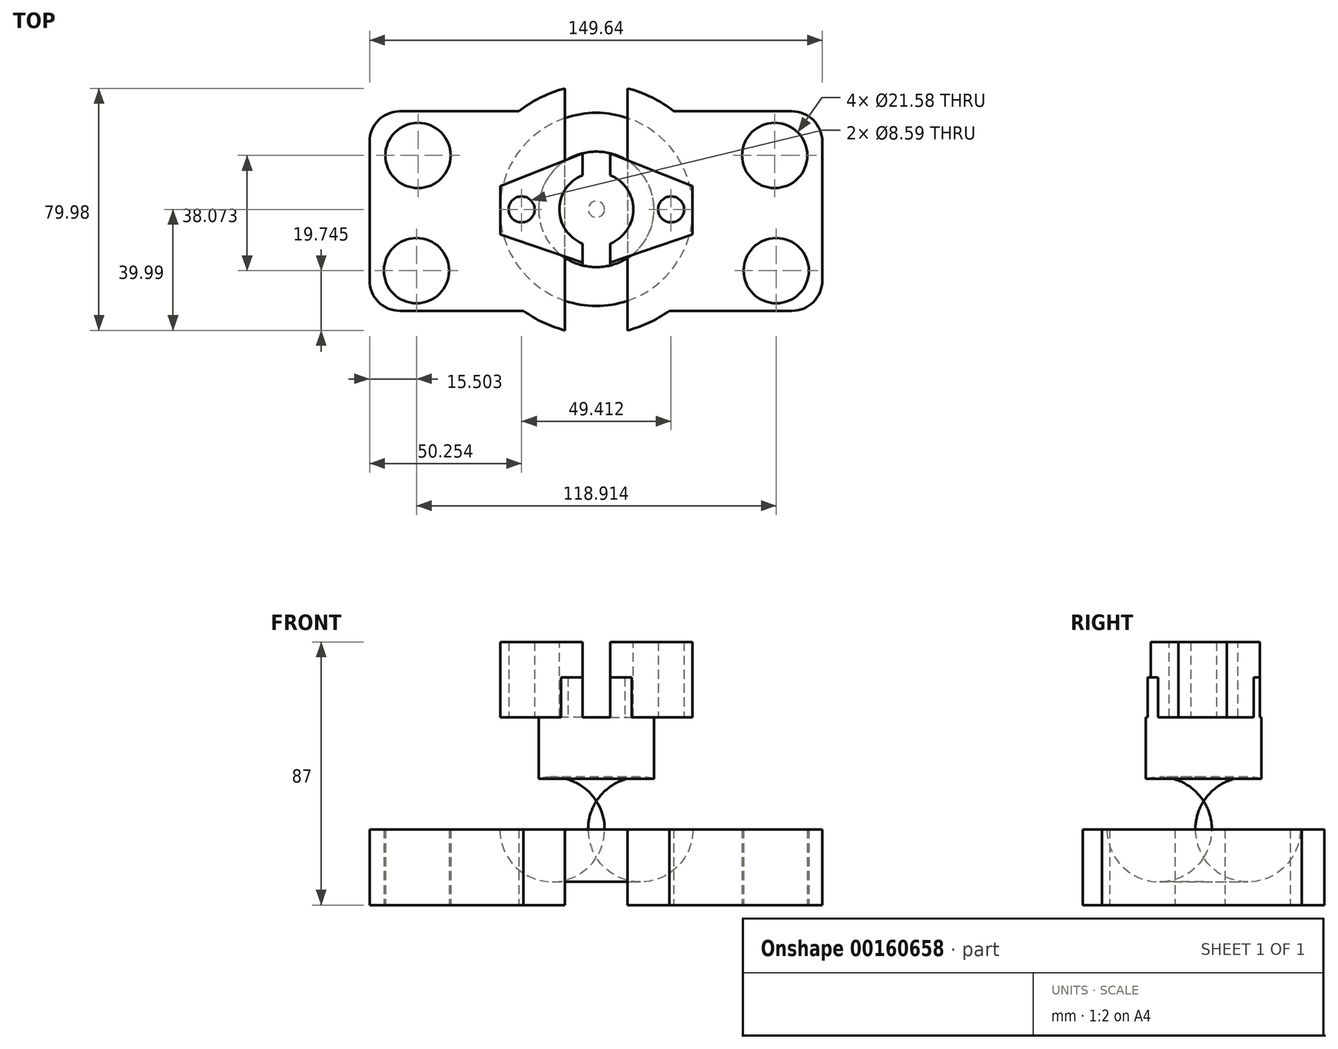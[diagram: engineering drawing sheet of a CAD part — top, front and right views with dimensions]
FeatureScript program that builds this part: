
annotation { "Feature Type Name" : "Feature", "Feature Type Description" : "" }
export const myFeature = defineFeature(function(context is Context, id is Id, definition is map)
    precondition{}
    {
        {
            var Q0;
            Q0=qCreatedBy(makeId("Top.planeOp"),FACE);
            var sketch = newSketch(context, id + "F0", { "sketchPlane" : qUnion([Q0])});
            skCircle(sketch, "E0", {"center": v(0, 0) * mm, "radius": 41.3 * mm});
            skLineSegment(sketch, "E1.bottom", {"start": v(-74.96, 32.43) * mm, "end": v(74.68, 32.43) * mm});
            skLineSegment(sketch, "E1.top", {"start": v(-74.96, -33.55) * mm, "end": v(74.68, -33.55) * mm});
            skLineSegment(sketch, "E1.left", {"start": v(-74.96, 32.43) * mm, "end": v(-74.96, -33.55) * mm});
            skLineSegment(sketch, "E1.right", {"start": v(74.68, 32.43) * mm, "end": v(74.68, -33.55) * mm});
            skCircle(sketch, "E2", {"center": v(-58.96, 17.83) * mm, "radius": 10.79 * mm});
            skCircle(sketch, "E3", {"center": v(-59.46, -20.25) * mm, "radius": 10.79 * mm});
            skCircle(sketch, "E4.MirrorC", {"center": v(59.46, -20.25) * mm, "radius": 10.79 * mm});
            skCircle(sketch, "E5.MirrorC", {"center": v(58.96, 17.83) * mm, "radius": 10.79 * mm});
            skLineSegment(sketch, "E6", {"start": v(-10.36, 40) * mm, "end": v(-10.36, 0) * mm});
            skLineSegment(sketch, "E7.MirrorCS", {"start": v(10.36, 40) * mm, "end": v(10.36, 0) * mm});
            skLineSegment(sketch, "E8", {"start": v(-10.36, 0) * mm, "end": v(10.36, 0) * mm});
            skLineSegment(sketch, "E9.MirrorCS", {"start": v(-10.36, -40) * mm, "end": v(-10.36, 0) * mm});
            skLineSegment(sketch, "E10.MirrorCS", {"start": v(10.36, -40) * mm, "end": v(10.36, 0) * mm});
            skSolve(sketch);
        }
        {
            var Q0;
            {var subQ0=sQuery(id+"F0.wireOp",EDGE,"E1.left");Q0=makeQuery(id+"F0.imprint","IMPRINT",FACE,{"disambiguationData":[TD([[makeQuery(id+"F0.imprint","IMPRINT",EDGE,{"derivedFrom":subQ0}),1.0]])]});}
            var Q1;
            {var subQ1=sQuery(id+"F0.wireOp",EDGE,"E0");var subQ7=sQuery(id+"F0.wireOp",EDGE,"E1.bottom");var subQ9=makeQuery(id+"F0.imprint","INTERSECT",VERTEX,{"disambiguationData":[OD(1.0)],"derivedFrom":[subQ1,subQ7]});Q1=makeQuery(id+"F0.imprint","IMPRINT",FACE,{"disambiguationData":[TD([[makeQuery(id+"F0.imprint","IMPRINT",EDGE,{"disambiguationData":[TD([[subQ9,-1.0]])],"derivedFrom":subQ1}),1.0]])]});}
            var Q2;
            {var subQ3=sQuery(id+"F0.wireOp",EDGE,"E1.bottom");var subQ6=sQuery(id+"F0.wireOp",EDGE,"E0");var subQ9=makeQuery(id+"F0.imprint","INTERSECT",VERTEX,{"disambiguationData":[OD(0.0)],"derivedFrom":[subQ6,subQ3]});Q2=makeQuery(id+"F0.imprint","IMPRINT",FACE,{"disambiguationData":[TD([[makeQuery(id+"F0.imprint","IMPRINT",EDGE,{"disambiguationData":[TD([[subQ9,1.0]])],"derivedFrom":subQ6}),1.0]])]});}
            var Q3;
            {var subQ0=sQuery(id+"F0.wireOp",EDGE,"E9.MirrorCS");var subQ1=sQuery(id+"F0.wireOp",EDGE,"E0");var subQ2=makeQuery(id+"F0.imprint","INTERSECT",VERTEX,{"derivedFrom":[subQ1,subQ0]});Q3=makeQuery(id+"F0.imprint","IMPRINT",FACE,{"disambiguationData":[TD([[makeQuery(id+"F0.imprint","IMPRINT",EDGE,{"disambiguationData":[TD([[subQ2,1.0]])],"derivedFrom":subQ1}),1.0]])]});}
            var Q4;
            {var subQ0=sQuery(id+"F0.wireOp",EDGE,"E10.MirrorCS");var subQ1=sQuery(id+"F0.wireOp",EDGE,"E0");var subQ2=makeQuery(id+"F0.imprint","INTERSECT",VERTEX,{"derivedFrom":[subQ1,subQ0]});Q4=makeQuery(id+"F0.imprint","IMPRINT",FACE,{"disambiguationData":[TD([[makeQuery(id+"F0.imprint","IMPRINT",EDGE,{"disambiguationData":[TD([[subQ2,-1.0]])],"derivedFrom":subQ1}),1.0]])]});}
            var Q5;
            {var subQ0=sQuery(id+"F0.wireOp",EDGE,"E6");var subQ1=sQuery(id+"F0.wireOp",EDGE,"E0");var subQ2=makeQuery(id+"F0.imprint","INTERSECT",VERTEX,{"derivedFrom":[subQ1,subQ0]});Q5=makeQuery(id+"F0.imprint","IMPRINT",FACE,{"disambiguationData":[TD([[makeQuery(id+"F0.imprint","IMPRINT",EDGE,{"disambiguationData":[TD([[subQ2,-1.0]])],"derivedFrom":subQ1}),1.0]])]});}
            var Q6;
            {var subQ0=sQuery(id+"F0.wireOp",EDGE,"E7.MirrorCS");var subQ1=sQuery(id+"F0.wireOp",EDGE,"E0");var subQ2=makeQuery(id+"F0.imprint","INTERSECT",VERTEX,{"derivedFrom":[subQ1,subQ0]});Q6=makeQuery(id+"F0.imprint","IMPRINT",FACE,{"disambiguationData":[TD([[makeQuery(id+"F0.imprint","IMPRINT",EDGE,{"disambiguationData":[TD([[subQ2,1.0]])],"derivedFrom":subQ1}),1.0]])]});}
            var Q7;
            {var subQ0=sQuery(id+"F0.wireOp",EDGE,"E1.right");Q7=makeQuery(id+"F0.imprint","IMPRINT",FACE,{"disambiguationData":[TD([[makeQuery(id+"F0.imprint","IMPRINT",EDGE,{"derivedFrom":subQ0}),-1.0]])]});}
            extrude(context, id + "F1", {"entities" : qUnion([Q0, Q1, Q2, Q3, Q4, Q5, Q6, Q7]), "depth" : 25 * mm});
        }
        {
            var Q0;
            Q0=makeQuery(id+"F1.opExtrude","SWEPT_EDGE",EDGE,{"disambiguationData":[OSD([sQuery(id+"F0.wireOp",EDGE,"E1.top"),sQuery(id+"F0.wireOp",EDGE,"E1.left")])]});
            var Q1;
            Q1=makeQuery(id+"F1.opExtrude","SWEPT_EDGE",EDGE,{"disambiguationData":[OSD([sQuery(id+"F0.wireOp",EDGE,"E1.bottom"),sQuery(id+"F0.wireOp",EDGE,"E1.left")])]});
            var Q2;
            Q2=makeQuery(id+"F1.opExtrude","SWEPT_EDGE",EDGE,{"disambiguationData":[OSD([sQuery(id+"F0.wireOp",EDGE,"E1.bottom"),sQuery(id+"F0.wireOp",EDGE,"E1.right")])]});
            var Q3;
            Q3=makeQuery(id+"F1.opExtrude","SWEPT_EDGE",EDGE,{"disambiguationData":[OSD([sQuery(id+"F0.wireOp",EDGE,"E1.top"),sQuery(id+"F0.wireOp",EDGE,"E1.right")])]});
            fillet(context, id + "F2", {"entities" : qUnion([Q0, Q1, Q2, Q3]), "radius" : 10 * mm, "tangentPropagation" : true, "allowEdgeOverflow" : false});
        }
        {
            var Q0;
            Q0=qCreatedBy(makeId("Right.planeOp"),FACE);
            var sketch = newSketch(context, id + "F3", { "sketchPlane" : qUnion([Q0])});
            skLineSegment(sketch, "E11.bottom", {"start": v(0, 24.9) * mm, "end": v(-19.1, 24.9) * mm});
            skLineSegment(sketch, "E11.top", {"start": v(0, 75.25) * mm, "end": v(-19.1, 75.25) * mm});
            skLineSegment(sketch, "E11.left", {"start": v(0, 24.9) * mm, "end": v(0, 75.25) * mm});
            skLineSegment(sketch, "E11.right", {"start": v(-19.1, 24.9) * mm, "end": v(-19.1, 75.25) * mm});
            skArc(sketch, "E12", {"start": v(-19.1, 41.73) * mm, "mid": v(-28.38, 35.5) * mm, "end": v(-31.93, 24.9) * mm});
            skLineSegment(sketch, "E13", {"start": v(-19.1, 24.9) * mm, "end": v(-31.93, 24.9) * mm});
            skSolve(sketch);
        }
        {
            var Q0;
            {var subQ1=sQuery(id+"F3.wireOp",EDGE,"E11.bottom");Q0=makeQuery(id+"F3.imprint","IMPRINT",FACE,{"disambiguationData":[TD([[makeQuery(id+"F3.imprint","IMPRINT",EDGE,{"derivedFrom":subQ1}),-1.0]])]});}
            var Q1;
            {var subQ2=sQuery(id+"F3.wireOp",EDGE,"E12");Q1=makeQuery(id+"F3.imprint","IMPRINT",FACE,{"disambiguationData":[TD([[makeQuery(id+"F3.imprint","IMPRINT",EDGE,{"derivedFrom":subQ2}),1.0]])]});}
            var Q2;
            Q2=sQuery(id+"F3.wireOp",EDGE,"E11.left");
            revolve(context, id + "F4", {"entities" : qUnion([Q0, Q1]), "axis" : qUnion([Q2]), "revolveType" : RevolveType.FULL});
        }
        {
            var Q0;
            Q0=makeQuery(id+"F4.opRevolve","SWEPT_FACE",FACE,{"disambiguationData":[OSD([sQuery(id+"F3.wireOp",EDGE,"E11.top")])]});
            var sketch = newSketch(context, id + "F5", { "sketchPlane" : qUnion([Q0])});
            skCircle(sketch, "E14", {"center": v(0, 0) * mm, "radius": 12.2 * mm});
            skLineSegment(sketch, "E15", {"start": v(-4.58, 11.32) * mm, "end": v(-4.58, 18.53) * mm});
            skLineSegment(sketch, "E16", {"start": v(4.58, 11.32) * mm, "end": v(4.58, 18.53) * mm});
            skLineSegment(sketch, "E17.MirrorCS", {"start": v(-4.58, -11.32) * mm, "end": v(-4.58, -18.53) * mm});
            skLineSegment(sketch, "E18.MirrorCS", {"start": v(4.58, -11.32) * mm, "end": v(4.58, -18.53) * mm});
            skSolve(sketch);
        }
        {
            var Q0;
            {var subQ0=sQuery(id+"F5.wireOp",EDGE,"E14");var subQ1=makeQuery(id+"F5.imprint","INTERSECT",VERTEX,{"derivedFrom":[subQ0,sQuery(id+"F5.wireOp",EDGE,"E15")]});Q0=makeQuery(id+"F5.imprint","IMPRINT",FACE,{"disambiguationData":[TD([[makeQuery(id+"F5.imprint","IMPRINT",EDGE,{"disambiguationData":[TD([[subQ1,1.0]])],"derivedFrom":subQ0}),1.0]])]});}
            var Q1;
            {var subQ0=sQuery(id+"F5.wireOp",EDGE,"E15");Q1=makeQuery(id+"F5.imprint","IMPRINT",FACE,{"disambiguationData":[TD([[makeQuery(id+"F5.imprint","IMPRINT",EDGE,{"derivedFrom":subQ0}),-1.0]])]});}
            var Q2;
            {var subQ0=sQuery(id+"F5.wireOp",EDGE,"E17.MirrorCS");Q2=makeQuery(id+"F5.imprint","IMPRINT",FACE,{"disambiguationData":[TD([[makeQuery(id+"F5.imprint","IMPRINT",EDGE,{"derivedFrom":subQ0}),1.0]])]});}
            extrude(context, id + "F6", {"entities" : qUnion([Q0, Q1, Q2]), "operationType" : NewBodyOperationType.REMOVE, "oppositeDirection" : true, "depth" : 13.25 * mm});
        }
        {
            var Q0;
            Q0=makeQuery(id+"F6.boolean.opBoolean","COPY",FACE,{"derivedFrom":makeQuery(id+"F6.opExtrude","CAP_FACE",FACE,{"disambiguationData":[OSD([sQuery(id+"F3.wireOp",EDGE,"E11.top"),sQuery(id+"F3.wireOp",EDGE,"E11.right"),sQuery(id+"F5.wireOp",EDGE,"E14"),sQuery(id+"F5.wireOp",EDGE,"E15"),sQuery(id+"F5.wireOp",EDGE,"E16"),sQuery(id+"F5.wireOp",EDGE,"E17.MirrorCS"),sQuery(id+"F5.wireOp",EDGE,"E18.MirrorCS")])],"isStart":false})});
            var sketch = newSketch(context, id + "F7", { "sketchPlane" : qUnion([Q0])});
            skLineSegment(sketch, "E19.left", {"start": v(19.12, 60.73) * mm, "end": v(19.12, 52.3) * mm});
            skLineSegment(sketch, "E20", {"start": v(-4.58, 18.53) * mm, "end": v(-31.72, 7.72) * mm});
            skLineSegment(sketch, "E21", {"start": v(-31.72, 7.72) * mm, "end": v(-31.72, -8.28) * mm});
            skLineSegment(sketch, "E22", {"start": v(-31.72, -8.28) * mm, "end": v(0, -19.1) * mm});
            skLineSegment(sketch, "E23.MirrorCS", {"start": v(4.58, 18.53) * mm, "end": v(31.72, 7.72) * mm});
            skLineSegment(sketch, "E24.MirrorCS", {"start": v(31.72, 7.72) * mm, "end": v(31.72, -8.28) * mm});
            skCircle(sketch, "E25", {"center": v(24.7, 0) * mm, "radius": 4.3 * mm});
            skCircle(sketch, "E26.MirrorC", {"center": v(-24.7, 0) * mm, "radius": 4.3 * mm});
            skLineSegment(sketch, "E27.MirrorCS", {"start": v(31.72, -8.28) * mm, "end": v(0, -19.1) * mm});
            skSolve(sketch);
        }
        {
            var Q0;
            Q0=makeQuery(id+"F7.imprint","IMPRINT",FACE,{"disambiguationData":[TD([[makeQuery(id+"F7.imprint","IMPRINT",EDGE,{"derivedFrom":sQuery(id+"F7.wireOp",EDGE,"E20")}),1.0]])]});
            var Q1;
            Q1=makeQuery(id+"F7.imprint","IMPRINT",FACE,{"disambiguationData":[TD([[makeQuery(id+"F7.imprint","IMPRINT",EDGE,{"derivedFrom":sQuery(id+"F7.wireOp",EDGE,"E23.MirrorCS")}),-1.0]])]});
            extrude(context, id + "F8", {"entities" : qUnion([Q0, Q1]), "operationType" : NewBodyOperationType.ADD, "depth" : 25 * mm});
        }
    });
